# Revit family: AD-81000_Revised
name_source: partatom
category: Plumbing Fixtures
revit_build: Autodesk Revit 2014 (Build: 20130308_1515(x64)
units: mm (PartAtom-declared; Revit-internal decimal feet)

## types (1)
- AD-81000
    ADA Compliant = Yes
    Assembly Code = D2010610
    CW Connection = Yes
    CWFU = 1.5
    Cold Water Connection Diameter = 3/8"
    Default Elevation = 34"
    Description = AER-DEC® 1-Station Wall-Mounted Sink
    ENC - Enclosure = Yes
    Finish = Stone-Sloan-DSC001-Designer White
    HW Connection = Yes
    HWFU = 1.5
    Hot Water Connection Diameter = 0"
    IAPMO Certification = UPC
    Manufacturer = Sloan Valve Company
    Material = Stone-Sloan-DSC001-Designer White
    Model = AD-81000
    Mounting = Wall Mounted
    Operation = Sensor-Activated
    Price = Prices may vary. Please consult Manufacturer Representative for most up-to-date price list.
    Product Page URL = https://www.sloan.com
    Revised Date = 02/07/2019
    URL = http://www.sloanvalve.com
    Vent Connection = No
    Voltage = 120 V
    WFU = 2
    Warrenty = 3 Year Limited
    Waste Connection = Yes
    Waste Connection Diameter = 1 1/4"

## geometry (parser evidence)
native form markers: Sweep x10
no freeform markers — native parametric forms only
